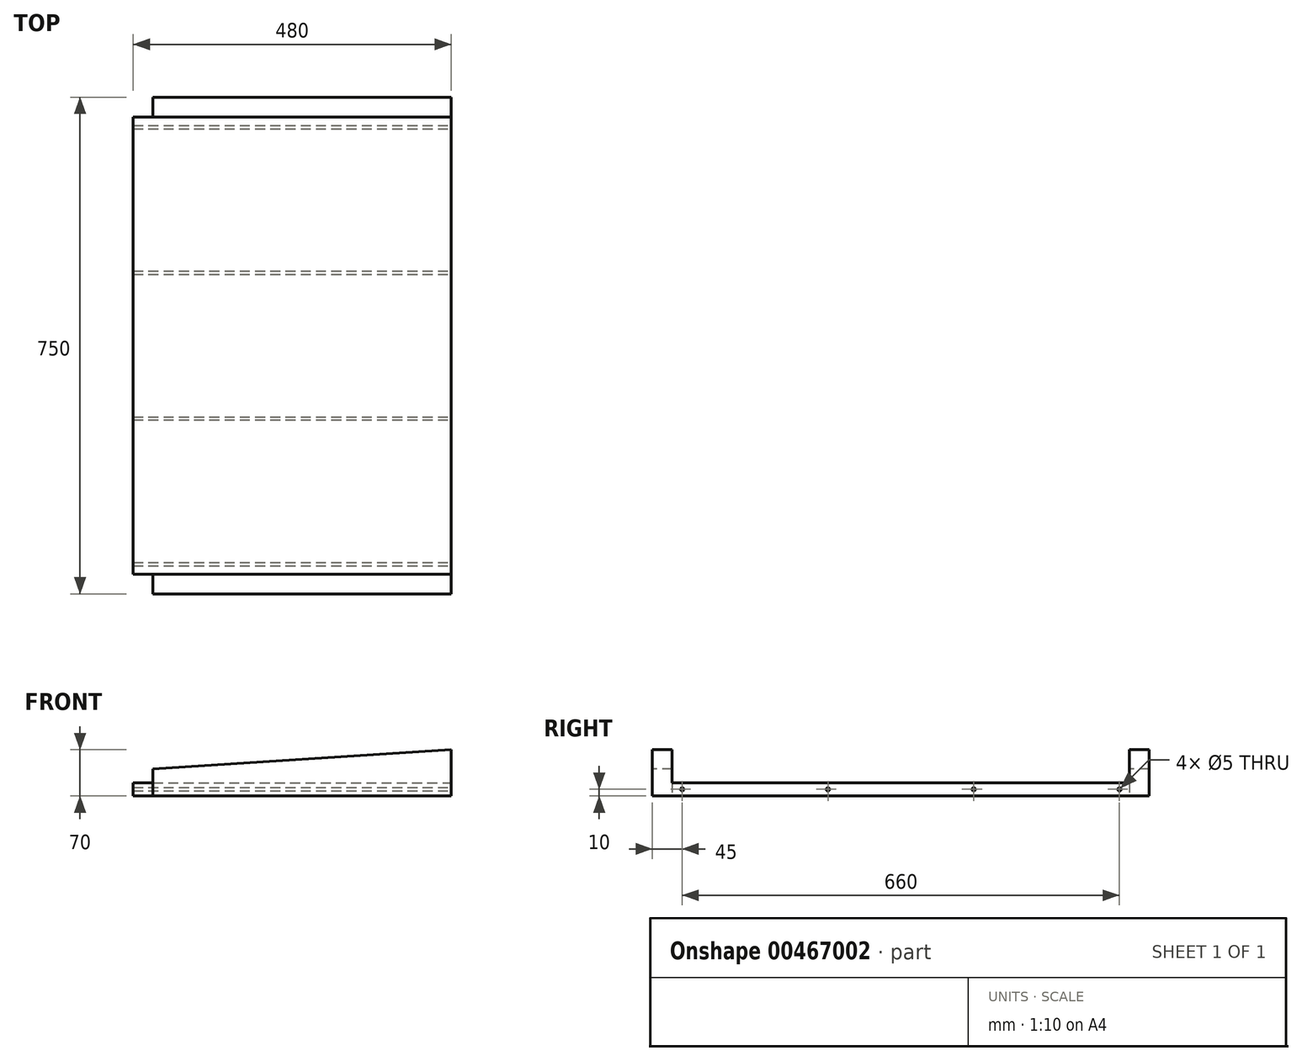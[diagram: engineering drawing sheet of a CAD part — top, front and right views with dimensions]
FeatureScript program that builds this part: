
annotation { "Feature Type Name" : "Feature", "Feature Type Description" : "" }
export const myFeature = defineFeature(function(context is Context, id is Id, definition is map)
    precondition{}
    {
        {
            var Q0;
            Q0=qCreatedBy(makeId("Top.planeOp"),FACE);
            var sketch = newSketch(context, id + "F0", { "sketchPlane" : qUnion([Q0])});
            skLineSegment(sketch, "E0.bottom", {"start": v(0, 0) * mm, "end": v(-460, 0) * mm});
            skLineSegment(sketch, "E0.top", {"start": v(0, -750) * mm, "end": v(-460, -750) * mm});
            skLineSegment(sketch, "E0.left", {"start": v(0, 0) * mm, "end": v(0, -750) * mm});
            skLineSegment(sketch, "E0.right", {"start": v(-460, 0) * mm, "end": v(-460, -750) * mm});
            skSolve(sketch);
        }
        {
            var Q0;
            Q0=makeQuery(id+"F0.imprint","IMPRINT",FACE,{"disambiguationData":[TD([[makeQuery(id+"F0.imprint","IMPRINT",EDGE,{"derivedFrom":sQuery(id+"F0.wireOp",EDGE,"E0.bottom")}),1.0]])]});
            extrude(context, id + "F1", {"entities" : qUnion([Q0]), "depth" : 20 * mm, "offsetDistance" : 25 * mm});
        }
        {
            var Q0;
            Q0=makeQuery(id+"F1.opExtrude","SWEPT_FACE",FACE,{"disambiguationData":[OSD([sQuery(id+"F0.wireOp",EDGE,"E0.left")])]});
            var sketch = newSketch(context, id + "F2", { "sketchPlane" : qUnion([Q0])});
            skLineSegment(sketch, "E1", {"start": v(-750, 10) * mm, "end": v(-705, 10) * mm});
            skPoint(sketch, "E2", {"position": v(-705, 10) * mm});
            skLineSegment(sketch, "E3", {"start": v(-705, 10) * mm, "end": v(-485, 10) * mm});
            skPoint(sketch, "E4", {"position": v(-485, 10) * mm});
            skLineSegment(sketch, "E5", {"start": v(-485, 10) * mm, "end": v(-265, 10) * mm});
            skLineSegment(sketch, "E6", {"start": v(-265, 10) * mm, "end": v(-45, 10) * mm});
            skLineSegment(sketch, "E7", {"start": v(-45, 10) * mm, "end": v(0, 10) * mm});
            skPoint(sketch, "E8", {"position": v(-265, 10) * mm});
            skPoint(sketch, "E9", {"position": v(-45, 10) * mm});
            skSolve(sketch);
        }
        {
            var Q0;
            Q0=sQuery(id+"F2.wireOp",VERTEX,"E2");
            var Q1;
            Q1=sQuery(id+"F2.wireOp",VERTEX,"E4");
            var Q2;
            Q2=sQuery(id+"F2.wireOp",VERTEX,"E8");
            var Q3;
            Q3=sQuery(id+"F2.wireOp",VERTEX,"E9");
            var Q4;
            Q4=makeQuery(id+"F1.opExtrude","SWEPT_BODY",BODY,{"disambiguationData":[OSD([sQuery(id+"F0.wireOp",EDGE,"E0.bottom"),sQuery(id+"F0.wireOp",EDGE,"E0.top"),sQuery(id+"F0.wireOp",EDGE,"E0.left"),sQuery(id+"F0.wireOp",EDGE,"E0.right")])]});
            hole(context, id + "F3", {"style" : HoleStyle.SIMPLE, "endStyle" : HoleEndStyle.THROUGH, "holeDiameter" : 5 * mm, "isTappedThrough" : true, "tappedDepth" : 12 * mm, "tapClearance" : 3, "locations" : qUnion([Q0, Q1, Q2, Q3]), "scope" : qUnion([Q4])});
        }
        {
            var Q0;
            Q0=makeQuery(id+"F1.opExtrude","CAP_FACE",FACE,{"disambiguationData":[OSD([sQuery(id+"F0.wireOp",EDGE,"E0.bottom"),sQuery(id+"F0.wireOp",EDGE,"E0.top"),sQuery(id+"F0.wireOp",EDGE,"E0.left"),sQuery(id+"F0.wireOp",EDGE,"E0.right")])],"isStart":false});
            var sketch = newSketch(context, id + "F4", { "sketchPlane" : qUnion([Q0])});
            skLineSegment(sketch, "E10.bottom", {"start": v(-460, -750) * mm, "end": v(0, -750) * mm});
            skLineSegment(sketch, "E10.top", {"start": v(-460, -720) * mm, "end": v(0, -720) * mm});
            skLineSegment(sketch, "E10.left", {"start": v(-460, -750) * mm, "end": v(-460, -720) * mm});
            skLineSegment(sketch, "E10.right", {"start": v(0, -750) * mm, "end": v(0, -720) * mm});
            skLineSegment(sketch, "E11.bottom", {"start": v(-460, 0) * mm, "end": v(0, 0) * mm});
            skLineSegment(sketch, "E11.top", {"start": v(-460, -30) * mm, "end": v(0, -30) * mm});
            skLineSegment(sketch, "E11.left", {"start": v(-460, 0) * mm, "end": v(-460, -30) * mm});
            skLineSegment(sketch, "E11.right", {"start": v(0, 0) * mm, "end": v(0, -30) * mm});
            skSolve(sketch);
        }
        {
            var Q0;
            Q0 = qSketchRegion(id + "F4", true);
            extrude(context, id + "F5", {"entities" : qUnion([Q0]), "operationType" : NewBodyOperationType.ADD, "depth" : 50 * mm, "offsetDistance" : 25 * mm});
        }
        {
            var Q0;
            Q0=makeQuery(id+"F5.boolean.opBoolean","MERGE",FACE,{"derivedFrom":[makeQuery(id+"F1.opExtrude","SWEPT_FACE",FACE,{"disambiguationData":[OSD([sQuery(id+"F0.wireOp",EDGE,"E0.bottom")])]}),makeQuery(id+"F5.opExtrude","SWEPT_FACE",FACE,{"disambiguationData":[OSD([sQuery(id+"F4.wireOp",EDGE,"E11.bottom")])]})]});
            var sketch = newSketch(context, id + "F6", { "sketchPlane" : qUnion([Q0])});
            skLineSegment(sketch, "E12", {"start": v(460, 0) * mm, "end": v(460, 40) * mm});
            skLineSegment(sketch, "E13", {"start": v(460, 40) * mm, "end": v(0, 70) * mm});
            skSolve(sketch);
        }
        {
            var Q0;
            Q0 = qSketchRegion(id + "F6", true);
            var Q1;
            {var subQ0=sQuery(id+"F6.wireOp",EDGE,"E13");Q1=makeQuery(id+"F6.imprint","IMPRINT",FACE,{"disambiguationData":[TD([[makeQuery(id+"F6.imprint","IMPRINT",EDGE,{"derivedFrom":subQ0}),-1.0]])]});}
            extrude(context, id + "F7", {"entities" : qUnion([Q0, Q1]), "operationType" : NewBodyOperationType.REMOVE, "oppositeDirection" : true, "depth" : 750 * mm, "offsetDistance" : 25 * mm});
        }
        {
            var Q0;
            Q0=makeQuery(id+"F5.boolean.opBoolean","MERGE",FACE,{"derivedFrom":[makeQuery(id+"F1.opExtrude","SWEPT_FACE",FACE,{"disambiguationData":[OSD([sQuery(id+"F0.wireOp",EDGE,"E0.right")])]}),makeQuery(id+"F5.opExtrude","SWEPT_FACE",FACE,{"disambiguationData":[OSD([sQuery(id+"F4.wireOp",EDGE,"E10.left")])]}),makeQuery(id+"F5.opExtrude","SWEPT_FACE",FACE,{"disambiguationData":[OSD([sQuery(id+"F4.wireOp",EDGE,"E11.left")])]})]});
            var sketch = newSketch(context, id + "F8", { "sketchPlane" : qUnion([Q0])});
            skLineSegment(sketch, "E14.bottom", {"start": v(0, 40) * mm, "end": v(30, 40) * mm});
            skLineSegment(sketch, "E14.top", {"start": v(0, 0) * mm, "end": v(30, 0) * mm});
            skLineSegment(sketch, "E14.left", {"start": v(0, 40) * mm, "end": v(0, 0) * mm});
            skLineSegment(sketch, "E14.right", {"start": v(30, 40) * mm, "end": v(30, 0) * mm});
            skLineSegment(sketch, "E15.bottom", {"start": v(750, 40) * mm, "end": v(720, 40) * mm});
            skLineSegment(sketch, "E15.top", {"start": v(750, 0) * mm, "end": v(720, 0) * mm});
            skLineSegment(sketch, "E15.left", {"start": v(750, 40) * mm, "end": v(750, 0) * mm});
            skLineSegment(sketch, "E15.right", {"start": v(720, 40) * mm, "end": v(720, 0) * mm});
            skSolve(sketch);
        }
        {
            var Q0;
            Q0 = qSketchRegion(id + "F8", true);
            extrude(context, id + "F9", {"entities" : qUnion([Q0]), "operationType" : NewBodyOperationType.REMOVE, "oppositeDirection" : true, "depth" : 10 * mm, "offsetDistance" : 25 * mm});
        }
        {
            var Q0;
            Q0=makeQuery(id+"F9.boolean.opBoolean","COPY",FACE,{"derivedFrom":makeQuery(id+"F9.opExtrude","SWEPT_FACE",FACE,{"disambiguationData":[OSD([sQuery(id+"F8.wireOp",EDGE,"E14.bottom")])]})});
            var Q1;
            Q1=makeQuery(id+"F9.boolean.opBoolean","COPY",FACE,{"derivedFrom":makeQuery(id+"F9.opExtrude","SWEPT_FACE",FACE,{"disambiguationData":[OSD([sQuery(id+"F8.wireOp",EDGE,"E15.bottom")])]})});
            extrude(context, id + "F10", {"entities" : qUnion([Q0, Q1]), "operationType" : NewBodyOperationType.REMOVE, "oppositeDirection" : true, "depth" : 25 * mm, "offsetDistance" : 25 * mm});
        }
        {
            var Q0;
            Q0=makeQuery(id+"F5.boolean.opBoolean","MERGE",FACE,{"derivedFrom":[makeQuery(id+"F1.opExtrude","SWEPT_FACE",FACE,{"disambiguationData":[OSD([sQuery(id+"F0.wireOp",EDGE,"E0.right")])]}),makeQuery(id+"F5.opExtrude","SWEPT_FACE",FACE,{"disambiguationData":[OSD([sQuery(id+"F4.wireOp",EDGE,"E10.left")])]}),makeQuery(id+"F5.opExtrude","SWEPT_FACE",FACE,{"disambiguationData":[OSD([sQuery(id+"F4.wireOp",EDGE,"E11.left")])]})]});
            extrude(context, id + "F11", {"entities" : qUnion([Q0]), "operationType" : NewBodyOperationType.ADD, "depth" : 20 * mm, "offsetDistance" : 25 * mm});
        }
    });
